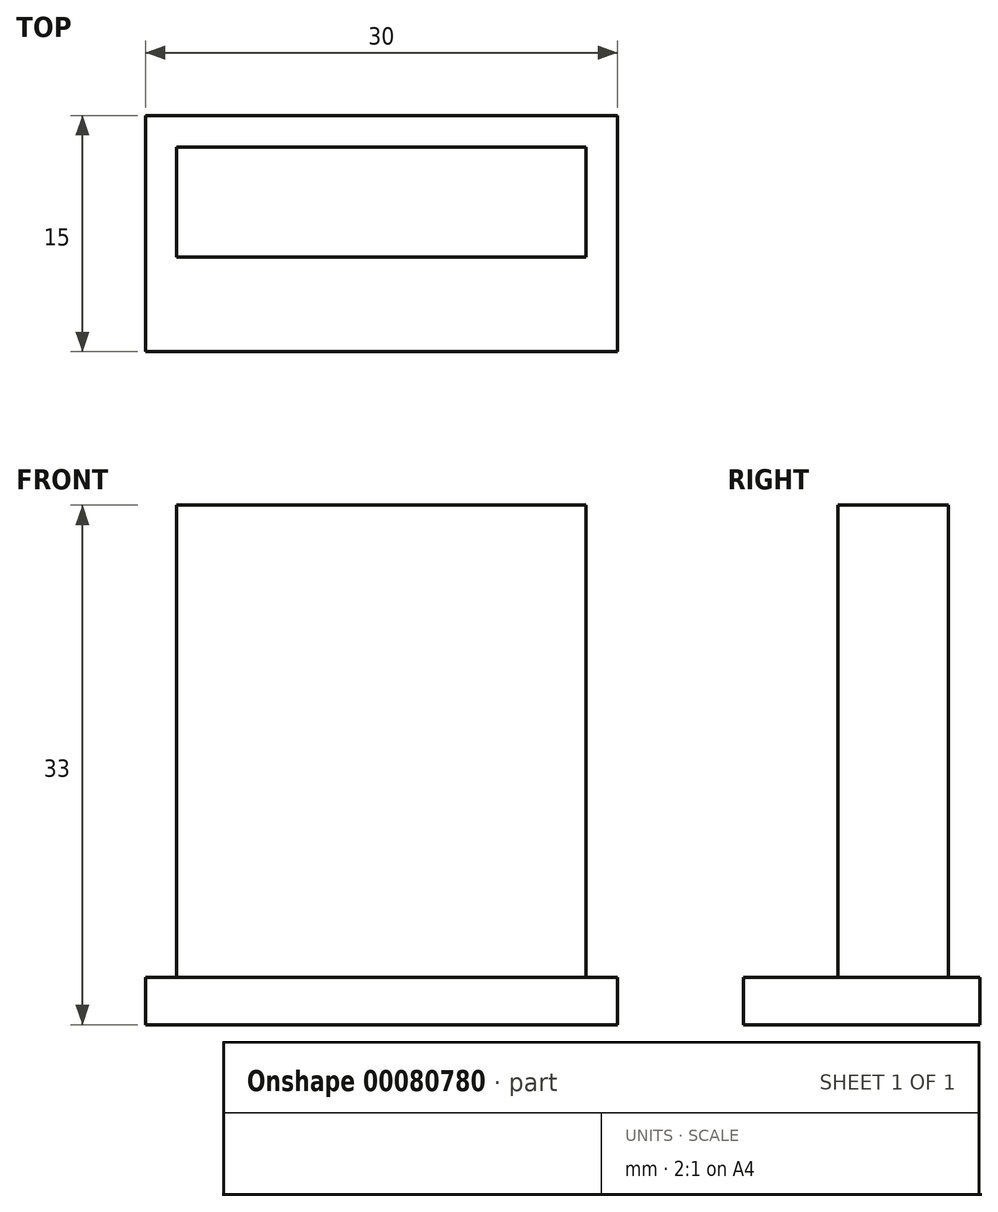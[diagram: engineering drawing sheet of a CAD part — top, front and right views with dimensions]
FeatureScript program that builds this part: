
annotation { "Feature Type Name" : "Feature", "Feature Type Description" : "" }
export const myFeature = defineFeature(function(context is Context, id is Id, definition is map)
    precondition{}
    {
        {
            var Q0;
            Q0=qCreatedBy(makeId("Front.planeOp"),FACE);
            var sketch = newSketch(context, id + "F0", { "sketchPlane" : qUnion([Q0])});
            skLineSegment(sketch, "E0.bottom", {"start": v(-13, 0) * mm, "end": v(13, 0) * mm});
            skLineSegment(sketch, "E0.top", {"start": v(-13, 30) * mm, "end": v(13, 30) * mm});
            skLineSegment(sketch, "E0.left", {"start": v(-13, 0) * mm, "end": v(-13, 30) * mm});
            skLineSegment(sketch, "E0.right", {"start": v(13, 0) * mm, "end": v(13, 30) * mm});
            skPoint(sketch, "E1", {"position": v(0, 0) * mm});
            skSolve(sketch);
        }
        {
            var Q0;
            Q0=makeQuery(id+"F0.imprint","IMPRINT",FACE,{"disambiguationData":[TD([[makeQuery(id+"F0.imprint","IMPRINT",EDGE,{"derivedFrom":sQuery(id+"F0.wireOp",EDGE,"E0.bottom")}),1.0]])]});
            extrude(context, id + "F1", {"entities" : qUnion([Q0]), "depth" : 7 * mm});
        }
        {
            var Q0;
            Q0=qCreatedBy(makeId("Top.planeOp"),FACE);
            var sketch = newSketch(context, id + "F2", { "sketchPlane" : qUnion([Q0])});
            skLineSegment(sketch, "E2.bottom", {"start": v(-15, 2) * mm, "end": v(15, 2) * mm});
            skLineSegment(sketch, "E2.top", {"start": v(-15, -13) * mm, "end": v(15, -13) * mm});
            skLineSegment(sketch, "E2.left", {"start": v(-15, 2) * mm, "end": v(-15, -13) * mm});
            skLineSegment(sketch, "E2.right", {"start": v(15, 2) * mm, "end": v(15, -13) * mm});
            skSolve(sketch);
        }
        {
            var Q0;
            Q0=makeQuery(id+"F2.imprint","IMPRINT",FACE,{"disambiguationData":[TD([[makeQuery(id+"F2.imprint","IMPRINT",EDGE,{"derivedFrom":sQuery(id+"F2.wireOp",EDGE,"E2.bottom")}),-1.0]])]});
            extrude(context, id + "F3", {"entities" : qUnion([Q0]), "operationType" : NewBodyOperationType.ADD, "oppositeDirection" : true, "depth" : 3 * mm});
        }
    });
